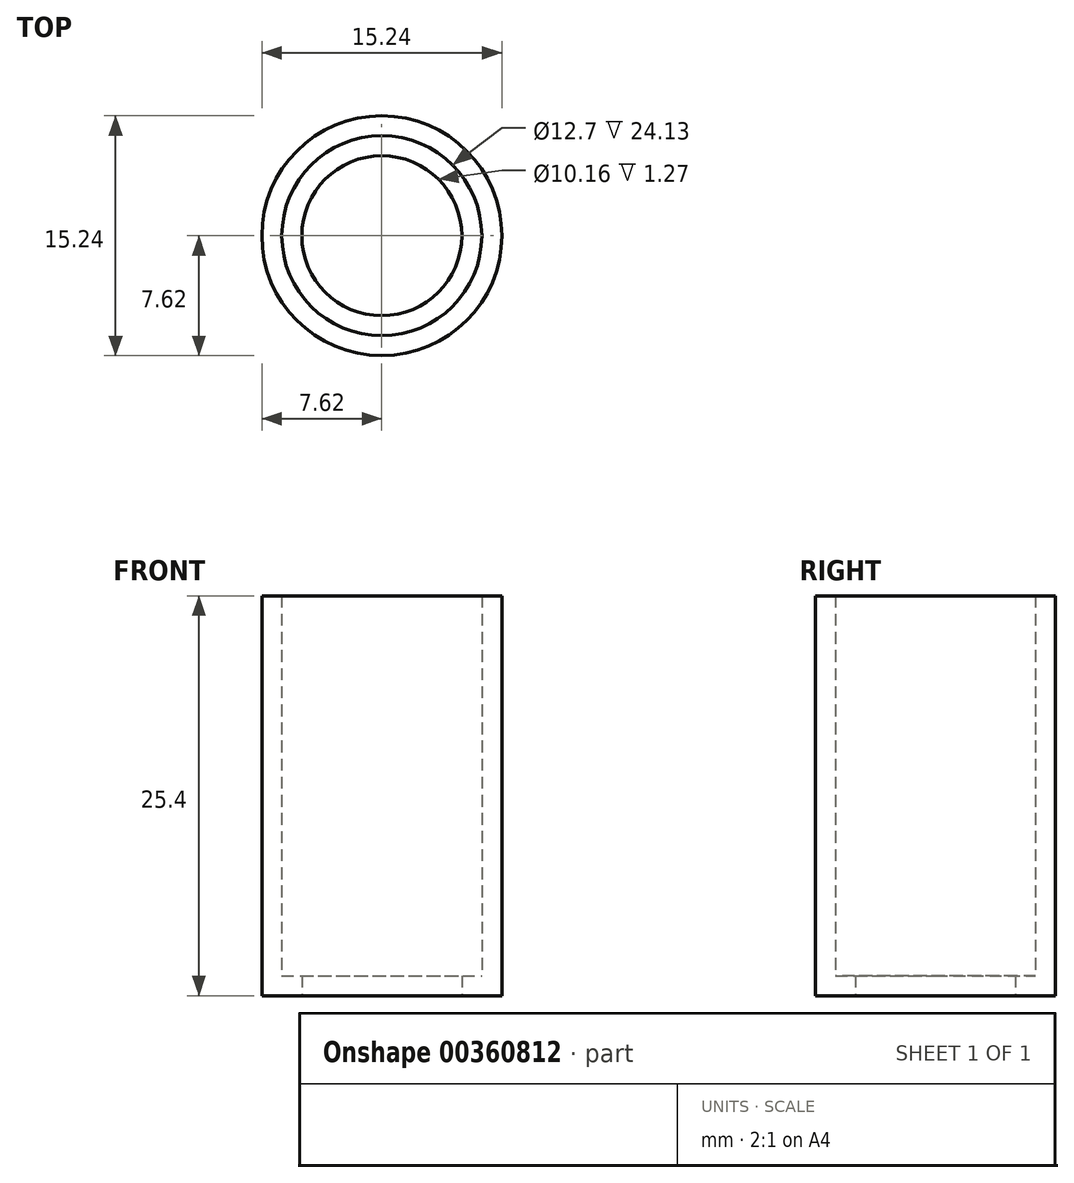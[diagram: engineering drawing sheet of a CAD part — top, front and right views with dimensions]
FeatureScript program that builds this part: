
annotation { "Feature Type Name" : "Feature", "Feature Type Description" : "" }
export const myFeature = defineFeature(function(context is Context, id is Id, definition is map)
    precondition{}
    {
        {
            var Q0;
            Q0=qCreatedBy(makeId("Front.planeOp"),FACE);
            var sketch = newSketch(context, id + "F0", { "sketchPlane" : qUnion([Q0])});
            skLineSegment(sketch, "E0.bottom", {"start": v(5.08, 0) * mm, "end": v(7.62, 0) * mm});
            skLineSegment(sketch, "E0.top", {"start": v(6.35, 25.4) * mm, "end": v(7.62, 25.4) * mm});
            skLineSegment(sketch, "E0.left", {"start": v(0, 0) * mm, "end": v(0, 25.4) * mm});
            skLineSegment(sketch, "E0.right", {"start": v(7.62, 0) * mm, "end": v(7.62, 25.4) * mm});
            skLineSegment(sketch, "E1", {"start": v(6.35, 25.4) * mm, "end": v(6.35, 1.27) * mm});
            skLineSegment(sketch, "E2.bottom", {"start": v(5.08, 1.27) * mm, "end": v(6.35, 1.27) * mm});
            skLineSegment(sketch, "E2.top", {"start": v(5.08, 0) * mm, "end": v(6.35, 0) * mm});
            skLineSegment(sketch, "E2.left", {"start": v(0, 1.27) * mm, "end": v(0, 0) * mm});
            skLineSegment(sketch, "E3", {"start": v(5.08, 1.27) * mm, "end": v(5.08, 0) * mm});
            skSolve(sketch);
        }
        {
            var Q0;
            Q0=makeQuery(id+"F0.imprint","IMPRINT",FACE,{"disambiguationData":[TD([[makeQuery(id+"F0.imprint","IMPRINT",EDGE,{"derivedFrom":sQuery(id+"F0.wireOp",EDGE,"E0.bottom")}),1.0]])]});
            var Q1;
            Q1=sQuery(id+"F0.wireOp",EDGE,"E0.left");
            revolve(context, id + "F1", {"entities" : qUnion([Q0]), "axis" : qUnion([Q1]), "revolveType" : RevolveType.FULL});
        }
    });
